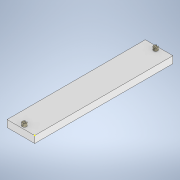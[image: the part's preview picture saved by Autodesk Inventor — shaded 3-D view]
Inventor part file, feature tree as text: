
AUTODESK INVENTOR PART (.ipt)
format: ipt  version: 2021 (Build 250183000, 183)  size: 128,512 bytes
history: native  units: mm
features: sketch x7, extrude x3, pattern_linear x1
ambient origin geometry x8: Origin, YZ Plane, XZ Plane, XY Plane, X Axis, Y Axis, Z Axis, Center Point
bodies: Solid1 (feature_tree)
feature tree (11):
  extrude  "Extrusion1"  Depth=100.0mm
  sketch  "Sketch2"  dims[d2=5.0mm d3=0.0mm d4=3.0mm]
  sketch  "Sketch3"  dims[d5=2.0mm d6=0.0mm d7=1.0mm]
  sketch  "Sketch4"  dims[d8=3.0mm]
  sketch  "Sketch5"  dims[d9=1.5mm d10=0.0mm d11=20.0mm d13=95.0mm]
  extrude  "Extrusion2"  Depth=5.0mm
  extrude  "Extrusion3"  Depth=1.0mm
  pattern_linear  "Rectangular Pattern1"  Count1=2 Spacing1=95.0mm
  sketch  "Sketch1"  dims[d0=20.0mm d1=100.0mm]
  sketch  "Sketch6"
  sketch  "Sketch7"
